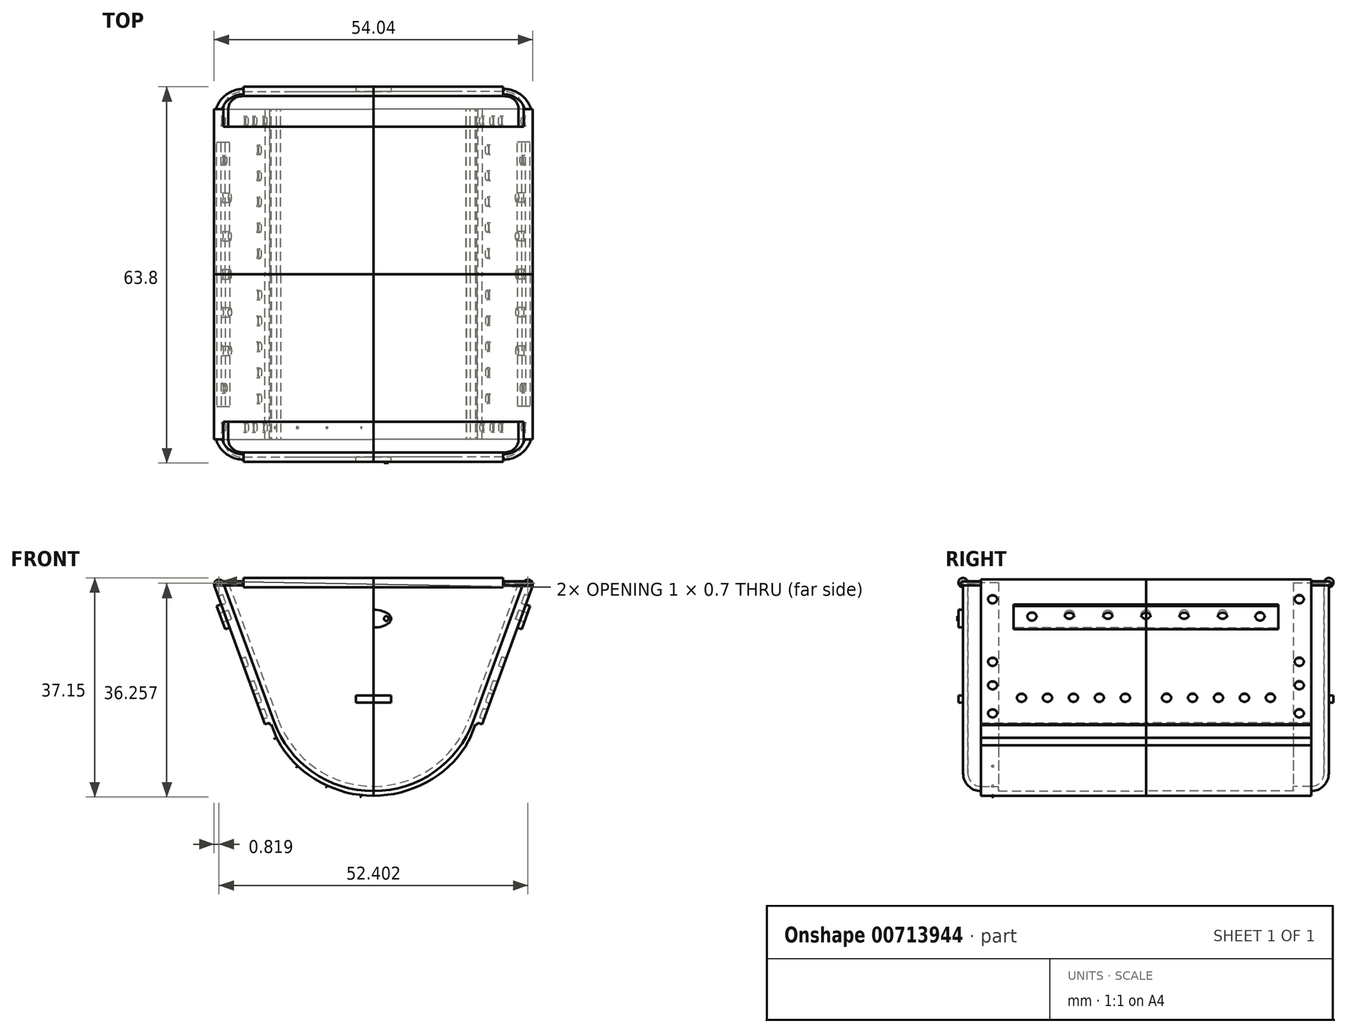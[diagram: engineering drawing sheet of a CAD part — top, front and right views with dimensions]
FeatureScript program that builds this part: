
annotation { "Feature Type Name" : "Feature", "Feature Type Description" : "" }
export const myFeature = defineFeature(function(context is Context, id is Id, definition is map)
    precondition{}
    {
        {
            var Q0;
            Q0=qCreatedBy(makeId("Right.planeOp"),FACE);
            var sketch = newSketch(context, id + "F0", { "sketchPlane" : qUnion([Q0])});
            skLineSegment(sketch, "E0.bottom", {"start": v(-15, -21) * mm, "end": v(-15, -21.8) * mm});
            skLineSegment(sketch, "E0.top", {"start": v(13, -21) * mm, "end": v(13, -21.8) * mm});
            skLineSegment(sketch, "E0.left", {"start": v(-15, -21) * mm, "end": v(13, -21) * mm});
            skLineSegment(sketch, "E0.right", {"start": v(-15, -21.8) * mm, "end": v(13, -21.8) * mm});
            skLineSegment(sketch, "E1.bottom", {"start": v(-15, -21) * mm, "end": v(-15, -20.2) * mm});
            skLineSegment(sketch, "E1.top", {"start": v(-12, -21) * mm, "end": v(-12, -20.2) * mm});
            skLineSegment(sketch, "E1.left", {"start": v(-15, -21) * mm, "end": v(-12, -21) * mm});
            skLineSegment(sketch, "E1.right", {"start": v(-15, -20.2) * mm, "end": v(-12, -20.2) * mm});
            skLineSegment(sketch, "E2.bottom", {"start": v(-15, -21) * mm, "end": v(-15, -18) * mm, "construction": true});
            skLineSegment(sketch, "E2.top", {"start": v(-15.62, -21) * mm, "end": v(-15.62, -18) * mm, "construction": true});
            skLineSegment(sketch, "E2.left", {"start": v(-15, -21) * mm, "end": v(-15.62, -21) * mm, "construction": true});
            skLineSegment(sketch, "E2.right", {"start": v(-15, -18) * mm, "end": v(-15.62, -18) * mm, "construction": true});
            skArc(sketch, "E3", {"start": v(-15, -21) * mm, "mid": v(-17.12, -20.12) * mm, "end": v(-18, -18) * mm});
            skArc(sketch, "E4", {"start": v(-15, -20.2) * mm, "mid": v(-16.56, -19.56) * mm, "end": v(-17.2, -18) * mm});
            skLineSegment(sketch, "E5.bottom", {"start": v(-17.2, -18) * mm, "end": v(-17.2, -3) * mm});
            skLineSegment(sketch, "E5.top", {"start": v(-18, -18) * mm, "end": v(-18, -3) * mm});
            skLineSegment(sketch, "E5.left", {"start": v(-17.2, -18) * mm, "end": v(-18, -18) * mm});
            skLineSegment(sketch, "E5.right", {"start": v(-17.2, -3) * mm, "end": v(-18, -3) * mm});
            skSolve(sketch);
        }
        {
            var Q0;
            Q0=makeQuery(id+"F0.imprint","IMPRINT",FACE,{"disambiguationData":[TD([[makeQuery(id+"F0.imprint","IMPRINT",EDGE,{"derivedFrom":sQuery(id+"F0.wireOp",EDGE,"E5.bottom")}),1.0]])]});
            var Q1;
            Q1=makeQuery(id+"F0.imprint","IMPRINT",FACE,{"disambiguationData":[TD([[makeQuery(id+"F0.imprint","IMPRINT",EDGE,{"derivedFrom":sQuery(id+"F0.wireOp",EDGE,"E1.bottom")}),1.0]])]});
            var Q2;
            Q2=makeQuery(id+"F0.imprint","IMPRINT",FACE,{"disambiguationData":[TD([[makeQuery(id+"F0.imprint","IMPRINT",EDGE,{"derivedFrom":sQuery(id+"F0.wireOp",EDGE,"E1.bottom")}),-1.0]])]});
            var Q3;
            Q3=makeQuery(id+"F0.imprint","IMPRINT",FACE,{"disambiguationData":[TD([[makeQuery(id+"F0.imprint","IMPRINT",EDGE,{"derivedFrom":sQuery(id+"F0.wireOp",EDGE,"E0.bottom")}),1.0]])]});
            var Q4;
            Q4=sQuery(id+"F0.wireOp",EDGE,"E5.right");
            revolve(context, id + "F1", {"surfaceOperationType" : NewSurfaceOperationType.NEW, "entities" : qUnion([Q0, Q1, Q2, Q3]), "axis" : qUnion([Q4]), "revolveType" : RevolveType.ONE_DIRECTION, "oppositeDirection" : true, "angle" : 70 * degree});
        }
        {
            var Q0;
            Q0=makeQuery(id+"F1.opRevolve","CAP_FACE",FACE,{"disambiguationData":[OSD([sQuery(id+"F0.wireOp",EDGE,"E0.bottom"),sQuery(id+"F0.wireOp",EDGE,"E0.top"),sQuery(id+"F0.wireOp",EDGE,"E0.left"),sQuery(id+"F0.wireOp",EDGE,"E0.right"),sQuery(id+"F0.wireOp",EDGE,"E1.top"),sQuery(id+"F0.wireOp",EDGE,"E1.right"),sQuery(id+"F0.wireOp",EDGE,"E3"),sQuery(id+"F0.wireOp",EDGE,"E4"),sQuery(id+"F0.wireOp",EDGE,"E5.bottom"),sQuery(id+"F0.wireOp",EDGE,"E5.top"),sQuery(id+"F0.wireOp",EDGE,"E5.right")])],"isStart":false});
            extrude(context, id + "F2", {"entities" : qUnion([Q0]), "operationType" : NewBodyOperationType.ADD, "depth" : 25 * mm, "offsetDistance" : 25 * mm});
        }
        {
            var Q0;
            {var subQ0=sQuery(id+"F0.wireOp",EDGE,"E0.bottom");Q0=makeQuery(id+"F2.boolean.opBoolean","MERGE",FACE,{"derivedFrom":[makeQuery(id+"F1.opRevolve","SWEPT_FACE",FACE,{"disambiguationData":[OSD([subQ0])]}),makeQuery(id+"F2.opExtrude","SWEPT_FACE",FACE,{"disambiguationData":[OSD([subQ0])]})]});}
            var sketch = newSketch(context, id + "F3", { "sketchPlane" : qUnion([Q0])});
            skLineSegment(sketch, "E6", {"start": v(-26.22, 14.06) * mm, "end": v(-17.67, -9.43) * mm});
            skLineSegment(sketch, "E7", {"start": v(-17.67, -9.43) * mm, "end": v(-17.3, -9.3) * mm});
            skLineSegment(sketch, "E8", {"start": v(-26.22, 14.06) * mm, "end": v(-17.3, -9.3) * mm});
            skSolve(sketch);
        }
        {
            var Q0;
            Q0=makeQuery(id+"F3.imprint","IMPRINT",FACE,{"disambiguationData":[TD([[makeQuery(id+"F3.imprint","IMPRINT",EDGE,{"derivedFrom":sQuery(id+"F3.wireOp",EDGE,"E6")}),1.0]])]});
            extrude(context, id + "F4", {"entities" : qUnion([Q0]), "oppositeDirection" : true, "depth" : 28 * mm, "offsetDistance" : 25 * mm});
        }
        {
            var Q0;
            Q0=makeQuery(id+"F2.opExtrude","SWEPT_FACE",FACE,{"disambiguationData":[OSD([sQuery(id+"F0.wireOp",EDGE,"E0.right")])]});
            var sketch = newSketch(context, id + "F5", { "sketchPlane" : qUnion([Q0])});
            skLineSegment(sketch, "E9.left", {"start": v(-13, 18.82) * mm, "end": v(-13, 14.65) * mm});
            skCircle(sketch, "E10", {"center": v(-13, 16.74) * mm, "radius": 0.8 * mm});
            skCircle(sketch, "E11.MirrorC", {"center": v(13, -1.04) * mm, "radius": 0.8 * mm});
            skCircle(sketch, "E12.MirrorC", {"center": v(13, 19.56) * mm, "radius": 0.8 * mm});
            skCircle(sketch, "E13.MirrorC", {"center": v(8.1, 1.78) * mm, "radius": 0.8 * mm});
            skCircle(sketch, "E14.MirrorC", {"center": v(13, 8.27) * mm, "radius": 0.8 * mm});
            skCircle(sketch, "E15.MirrorC", {"center": v(6.33, 16.74) * mm, "radius": 0.8 * mm});
            skCircle(sketch, "E16.MirrorC", {"center": v(13, 4.02) * mm, "radius": 0.8 * mm});
            skLineSegment(sketch, "E17.MirrorCS", {"start": v(13, 20.36) * mm, "end": v(13, -1.84) * mm});
            skCircle(sketch, "E18.MirrorC", {"center": v(-0.02, 16.74) * mm, "radius": 0.8 * mm});
            skCircle(sketch, "E19.MirrorC", {"center": v(-0.7, 1.78) * mm, "radius": 0.8 * mm});
            skLineSegment(sketch, "E20.MirrorCS", {"start": v(9.43, 18.82) * mm, "end": v(9.43, 14.65) * mm});
            skCircle(sketch, "E21.MirrorC", {"center": v(-5.1, 1.78) * mm, "radius": 0.8 * mm});
            skCircle(sketch, "E22.MirrorC", {"center": v(-9.5, 1.78) * mm, "radius": 0.8 * mm});
            skCircle(sketch, "E23.MirrorC", {"center": v(-6.54, 16.74) * mm, "radius": 0.8 * mm});
            skCircle(sketch, "E24.MirrorC", {"center": v(13, 15.05) * mm, "radius": 0.8 * mm});
            skCircle(sketch, "E25.MirrorC", {"center": v(3.7, 1.78) * mm, "radius": 0.8 * mm});
            skLineSegment(sketch, "E26.MirrorCS", {"start": v(-13, 18.82) * mm, "end": v(9.43, 18.82) * mm});
            skLineSegment(sketch, "E27.MirrorCS", {"start": v(13, 19.36) * mm, "end": v(13, -2.82) * mm, "construction": true});
            skPoint(sketch, "E28.MirrorP", {"position": v(9.43, 16.74) * mm});
            skLineSegment(sketch, "E29.MirrorCS", {"start": v(-13, 1.78) * mm, "end": v(-27.66, 1.78) * mm, "construction": true});
            skLineSegment(sketch, "E30.MirrorCS", {"start": v(12.5, 1.78) * mm, "end": v(8.1, 1.78) * mm, "construction": true});
            skLineSegment(sketch, "E31.MirrorCS", {"start": v(-13, 14.65) * mm, "end": v(9.43, 14.65) * mm});
            skSolve(sketch);
        }
        {
            var Q0;
            Q0=makeQuery(id+"F5.imprint","IMPRINT",FACE,{"disambiguationData":[TD([[makeQuery(id+"F5.imprint","IMPRINT",EDGE,{"derivedFrom":sQuery(id+"F5.wireOp",EDGE,"E15.MirrorC")}),1.0]])]});
            extrude(context, id + "F6", {"entities" : qUnion([Q0]), "operationType" : NewBodyOperationType.ADD, "depth" : .8 * mm, "offsetDistance" : 25 * mm});
        }
        {
            var Q0;
            {var subQ0=sQuery(id+"F5.wireOp",EDGE,"E17.MirrorCS");var subQ1=sQuery(id+"F5.wireOp",EDGE,"E12.MirrorC");var subQ2=makeQuery(id+"F5.imprint","INTERSECT",VERTEX,{"disambiguationData":[OD(0.0)],"derivedFrom":[subQ1,subQ0]});Q0=makeQuery(id+"F5.imprint","IMPRINT",FACE,{"disambiguationData":[TD([[makeQuery(id+"F5.imprint","IMPRINT",EDGE,{"disambiguationData":[TD([[subQ2,1.0]])],"derivedFrom":subQ1}),-1.0]])]});}
            var Q1;
            {var subQ0=sQuery(id+"F5.wireOp",EDGE,"E17.MirrorCS");var subQ1=sQuery(id+"F5.wireOp",EDGE,"E12.MirrorC");var subQ2=makeQuery(id+"F5.imprint","INTERSECT",VERTEX,{"disambiguationData":[OD(0.0)],"derivedFrom":[subQ1,subQ0]});Q1=makeQuery(id+"F5.imprint","IMPRINT",FACE,{"disambiguationData":[TD([[makeQuery(id+"F5.imprint","IMPRINT",EDGE,{"disambiguationData":[TD([[subQ2,-1.0]])],"derivedFrom":subQ1}),-1.0]])]});}
            var Q2;
            {var subQ0=sQuery(id+"F5.wireOp",EDGE,"E24.MirrorC");var subQ1=sQuery(id+"F5.wireOp",EDGE,"E17.MirrorCS");var subQ2=makeQuery(id+"F5.imprint","INTERSECT",VERTEX,{"disambiguationData":[OD(0.0)],"derivedFrom":[subQ1,subQ0]});Q2=makeQuery(id+"F5.imprint","IMPRINT",FACE,{"disambiguationData":[TD([[makeQuery(id+"F5.imprint","IMPRINT",EDGE,{"disambiguationData":[TD([[subQ2,-1.0]])],"derivedFrom":subQ1}),-1.0]])]});}
            var Q3;
            {var subQ0=sQuery(id+"F5.wireOp",EDGE,"E24.MirrorC");var subQ1=sQuery(id+"F5.wireOp",EDGE,"E17.MirrorCS");var subQ2=makeQuery(id+"F5.imprint","INTERSECT",VERTEX,{"disambiguationData":[OD(0.0)],"derivedFrom":[subQ1,subQ0]});Q3=makeQuery(id+"F5.imprint","IMPRINT",FACE,{"disambiguationData":[TD([[makeQuery(id+"F5.imprint","IMPRINT",EDGE,{"disambiguationData":[TD([[subQ2,-1.0]])],"derivedFrom":subQ1}),1.0]])]});}
            var Q4;
            {var subQ0=sQuery(id+"F5.wireOp",EDGE,"E17.MirrorCS");var subQ1=sQuery(id+"F5.wireOp",EDGE,"E14.MirrorC");var subQ2=makeQuery(id+"F5.imprint","INTERSECT",VERTEX,{"disambiguationData":[OD(0.0)],"derivedFrom":[subQ1,subQ0]});Q4=makeQuery(id+"F5.imprint","IMPRINT",FACE,{"disambiguationData":[TD([[makeQuery(id+"F5.imprint","IMPRINT",EDGE,{"disambiguationData":[TD([[subQ2,1.0]])],"derivedFrom":subQ1}),-1.0]])]});}
            var Q5;
            {var subQ0=sQuery(id+"F5.wireOp",EDGE,"E17.MirrorCS");var subQ1=sQuery(id+"F5.wireOp",EDGE,"E14.MirrorC");var subQ2=makeQuery(id+"F5.imprint","INTERSECT",VERTEX,{"disambiguationData":[OD(0.0)],"derivedFrom":[subQ1,subQ0]});Q5=makeQuery(id+"F5.imprint","IMPRINT",FACE,{"disambiguationData":[TD([[makeQuery(id+"F5.imprint","IMPRINT",EDGE,{"disambiguationData":[TD([[subQ2,-1.0]])],"derivedFrom":subQ1}),-1.0]])]});}
            var Q6;
            {var subQ0=sQuery(id+"F5.wireOp",EDGE,"E17.MirrorCS");var subQ1=sQuery(id+"F5.wireOp",EDGE,"E16.MirrorC");var subQ2=makeQuery(id+"F5.imprint","INTERSECT",VERTEX,{"disambiguationData":[OD(0.0)],"derivedFrom":[subQ1,subQ0]});Q6=makeQuery(id+"F5.imprint","IMPRINT",FACE,{"disambiguationData":[TD([[makeQuery(id+"F5.imprint","IMPRINT",EDGE,{"disambiguationData":[TD([[subQ2,1.0]])],"derivedFrom":subQ1}),-1.0]])]});}
            var Q7;
            {var subQ0=sQuery(id+"F5.wireOp",EDGE,"E17.MirrorCS");var subQ1=sQuery(id+"F5.wireOp",EDGE,"E16.MirrorC");var subQ2=makeQuery(id+"F5.imprint","INTERSECT",VERTEX,{"disambiguationData":[OD(0.0)],"derivedFrom":[subQ1,subQ0]});Q7=makeQuery(id+"F5.imprint","IMPRINT",FACE,{"disambiguationData":[TD([[makeQuery(id+"F5.imprint","IMPRINT",EDGE,{"disambiguationData":[TD([[subQ2,-1.0]])],"derivedFrom":subQ1}),-1.0]])]});}
            var Q8;
            {var subQ0=sQuery(id+"F5.wireOp",EDGE,"E17.MirrorCS");var subQ1=sQuery(id+"F5.wireOp",EDGE,"E11.MirrorC");var subQ2=makeQuery(id+"F5.imprint","INTERSECT",VERTEX,{"disambiguationData":[OD(0.0)],"derivedFrom":[subQ1,subQ0]});Q8=makeQuery(id+"F5.imprint","IMPRINT",FACE,{"disambiguationData":[TD([[makeQuery(id+"F5.imprint","IMPRINT",EDGE,{"disambiguationData":[TD([[subQ2,-1.0]])],"derivedFrom":subQ1}),-1.0]])]});}
            var Q9;
            {var subQ0=sQuery(id+"F5.wireOp",EDGE,"E17.MirrorCS");var subQ1=sQuery(id+"F5.wireOp",EDGE,"E11.MirrorC");var subQ2=makeQuery(id+"F5.imprint","INTERSECT",VERTEX,{"disambiguationData":[OD(0.0)],"derivedFrom":[subQ1,subQ0]});Q9=makeQuery(id+"F5.imprint","IMPRINT",FACE,{"disambiguationData":[TD([[makeQuery(id+"F5.imprint","IMPRINT",EDGE,{"disambiguationData":[TD([[subQ2,1.0]])],"derivedFrom":subQ1}),-1.0]])]});}
            var Q10;
            Q10=makeQuery(id+"F5.imprint","IMPRINT",FACE,{"disambiguationData":[TD([[makeQuery(id+"F5.imprint","IMPRINT",EDGE,{"derivedFrom":sQuery(id+"F5.wireOp",EDGE,"E13.MirrorC")}),-1.0]])]});
            var Q11;
            Q11=makeQuery(id+"F5.imprint","IMPRINT",FACE,{"disambiguationData":[TD([[makeQuery(id+"F5.imprint","IMPRINT",EDGE,{"derivedFrom":sQuery(id+"F5.wireOp",EDGE,"E25.MirrorC")}),-1.0]])]});
            var Q12;
            Q12=makeQuery(id+"F5.imprint","IMPRINT",FACE,{"disambiguationData":[TD([[makeQuery(id+"F5.imprint","IMPRINT",EDGE,{"derivedFrom":sQuery(id+"F5.wireOp",EDGE,"E19.MirrorC")}),-1.0]])]});
            var Q13;
            Q13=makeQuery(id+"F5.imprint","IMPRINT",FACE,{"disambiguationData":[TD([[makeQuery(id+"F5.imprint","IMPRINT",EDGE,{"derivedFrom":sQuery(id+"F5.wireOp",EDGE,"E21.MirrorC")}),-1.0]])]});
            var Q14;
            Q14=makeQuery(id+"F5.imprint","IMPRINT",FACE,{"disambiguationData":[TD([[makeQuery(id+"F5.imprint","IMPRINT",EDGE,{"derivedFrom":sQuery(id+"F5.wireOp",EDGE,"E22.MirrorC")}),-1.0]])]});
            var Q15;
            Q15=makeQuery(id+"F5.imprint","IMPRINT",FACE,{"disambiguationData":[TD([[makeQuery(id+"F5.imprint","IMPRINT",EDGE,{"derivedFrom":sQuery(id+"F5.wireOp",EDGE,"E15.MirrorC")}),1.0]])]});
            extrude(context, id + "F7", {"entities" : qUnion([Q0, Q1, Q2, Q3, Q4, Q5, Q6, Q7, Q8, Q9, Q10, Q11, Q12, Q13, Q14, Q15]), "operationType" : NewBodyOperationType.ADD, "depth" : .8 * mm, "offsetDistance" : 25 * mm});
        }
        {
            var Q0;
            {var subQ0=sQuery(id+"F0.wireOp",EDGE,"E0.bottom");Q0=makeQuery(id+"F2.boolean.opBoolean","MERGE",FACE,{"derivedFrom":[makeQuery(id+"F1.opRevolve","SWEPT_FACE",FACE,{"disambiguationData":[OSD([subQ0])]}),makeQuery(id+"F2.opExtrude","SWEPT_FACE",FACE,{"disambiguationData":[OSD([subQ0])]})]});}
            var sketch = newSketch(context, id + "F8", { "sketchPlane" : qUnion([Q0])});
            skLineSegment(sketch, "E32", {"start": v(-26.22, 14.06) * mm, "end": v(-25.65, 14.27) * mm, "construction": true});
            skLineSegment(sketch, "E33", {"start": v(-26.22, 14.06) * mm, "end": v(-25.46, 14.34) * mm});
            skLineSegment(sketch, "E34", {"start": v(-26.22, 14.06) * mm, "end": v(-17.17, -10.79) * mm});
            skLineSegment(sketch, "E35", {"start": v(-25.46, 14.34) * mm, "end": v(-27.63, 13.55) * mm, "construction": true});
            skLineSegment(sketch, "E36", {"start": v(-27.63, 13.55) * mm, "end": v(-37.62, 13.34) * mm, "construction": true});
            skCircle(sketch, "E37", {"center": v(-26.22, 14.06) * mm, "radius": 0.8 * mm});
            skSolve(sketch);
        }
        {
            var Q0;
            Q0=makeQuery(id+"F8.imprint","IMPRINT",FACE,{"disambiguationData":[TD([[makeQuery(id+"F8.imprint","IMPRINT",EDGE,{"derivedFrom":sQuery(id+"F8.wireOp",EDGE,"LhP0sfN7-OzdZ-2R5g-prXg-6koaKuXarlO9")}),-1.0]])]});
            var Q1;
            Q1=makeQuery(id+"F8.imprint","IMPRINT",FACE,{"disambiguationData":[TD([[makeQuery(id+"F8.imprint","IMPRINT",EDGE,{"derivedFrom":sQuery(id+"F8.wireOp",EDGE,"LhP0sfN7-OzdZ-2R5g-prXg-6koaKuXarlO9")}),1.0]])]});
            var Q2;
            {var subQ0=sQuery(id+"F8.wireOp",EDGE,"E33");Q2=makeQuery(id+"F8.imprint","IMPRINT",FACE,{"disambiguationData":[TD([[makeQuery(id+"F8.imprint","IMPRINT",EDGE,{"derivedFrom":subQ0}),-1.0]])]});}
            extrude(context, id + "F9", {"entities" : qUnion([Q0, Q1, Q2]), "operationType" : NewBodyOperationType.ADD, "oppositeDirection" : true, "depth" : 28 * mm, "offsetDistance" : 25 * mm});
        }
        {
            var Q0;
            {var subQ0=sQuery(id+"F0.wireOp",EDGE,"E0.top");Q0=makeQuery(id+"F2.boolean.opBoolean","MERGE",FACE,{"derivedFrom":[makeQuery(id+"F1.opRevolve","SWEPT_FACE",FACE,{"disambiguationData":[OSD([subQ0])]}),makeQuery(id+"F2.opExtrude","SWEPT_FACE",FACE,{"disambiguationData":[OSD([subQ0])]})]});}
            var sketch = newSketch(context, id + "F10", { "sketchPlane" : qUnion([Q0])});
            skLineSegment(sketch, "E38.bottom", {"start": v(25.46, 14.34) * mm, "end": v(5.72, 14.34) * mm});
            skLineSegment(sketch, "E38.top", {"start": v(25.46, 20.8) * mm, "end": v(5.72, 20.8) * mm});
            skLineSegment(sketch, "E38.left", {"start": v(25.46, 14.34) * mm, "end": v(25.46, 20.8) * mm});
            skLineSegment(sketch, "E38.right", {"start": v(5.72, 14.34) * mm, "end": v(5.72, 20.8) * mm});
            skSolve(sketch);
        }
        {
            var Q0;
            {var subQ0=sQuery(id+"F0.wireOp",EDGE,"E5.top");Q0=makeQuery(id+"F2.boolean.opBoolean","MERGE",FACE,{"derivedFrom":[makeQuery(id+"F1.opRevolve","SWEPT_FACE",FACE,{"disambiguationData":[OSD([subQ0])]}),makeQuery(id+"F2.opExtrude","SWEPT_FACE",FACE,{"disambiguationData":[OSD([subQ0])]})]});}
            var sketch = newSketch(context, id + "F11", { "sketchPlane" : qUnion([Q0])});
            skLineSegment(sketch, "E39.bottom", {"start": v(0, -3) * mm, "end": v(-6.31, -3) * mm});
            skLineSegment(sketch, "E39.top", {"start": v(0, 14.34) * mm, "end": v(-6.31, 14.34) * mm});
            skLineSegment(sketch, "E39.left", {"start": v(0, -3) * mm, "end": v(0, 14.34) * mm});
            skLineSegment(sketch, "E39.right", {"start": v(-6.31, -3) * mm, "end": v(-6.31, 14.34) * mm});
            skSolve(sketch);
        }
        {
            var Q0;
            {var subQ0=sQuery(id+"F11.wireOp",EDGE,"E39.top");Q0=makeQuery(id+"F11.imprint","IMPRINT",FACE,{"disambiguationData":[TD([[makeQuery(id+"F11.imprint","IMPRINT",EDGE,{"derivedFrom":subQ0}),1.0]])]});}
            extrude(context, id + "F12", {"entities" : qUnion([Q0]), "operationType" : NewBodyOperationType.ADD, "oppositeDirection" : true, "depth" : .8 * mm, "offsetDistance" : 25 * mm});
        }
        {
            var Q0;
            Q0=makeQuery(id+"F10.imprint","IMPRINT",FACE,{"disambiguationData":[TD([[makeQuery(id+"F10.imprint","IMPRINT",EDGE,{"derivedFrom":sQuery(id+"F10.wireOp",EDGE,"E38.bottom")}),-1.0]])]});
            extrude(context, id + "F13", {"entities" : qUnion([Q0]), "operationType" : NewBodyOperationType.REMOVE, "oppositeDirection" : true, "depth" : 50 * mm, "offsetDistance" : 25 * mm});
        }
        {
            var Q0;
            {var subQ0=sQuery(id+"F0.wireOp",EDGE,"E5.top");Q0=makeQuery(id+"F12.boolean.opBoolean","MERGE",FACE,{"derivedFrom":[makeQuery(id+"F2.boolean.opBoolean","MERGE",FACE,{"derivedFrom":[makeQuery(id+"F1.opRevolve","SWEPT_FACE",FACE,{"disambiguationData":[OSD([subQ0])]}),makeQuery(id+"F2.opExtrude","SWEPT_FACE",FACE,{"disambiguationData":[OSD([subQ0])]})]}),makeQuery(id+"F12.opExtrude","CAP_FACE",FACE,{"disambiguationData":[OSD([subQ0,sQuery(id+"F0.wireOp",EDGE,"E5.right"),sQuery(id+"F11.wireOp",EDGE,"E39.top"),sQuery(id+"F11.wireOp",EDGE,"E39.left")])],"isStart":true})]});}
            var sketch = newSketch(context, id + "F14", { "sketchPlane" : qUnion([Q0])});
            skEllipse(sketch, "E40", {"center": v(0, 8.24) * mm, "majorRadius": 3 * mm, "minorRadius": 1.5 * mm, "majorAxis": v(1, 0)});
            skCircle(sketch, "E41", {"center": v(2.18, 8.25) * mm, "radius": 0.4 * mm});
            skLineSegment(sketch, "E42.top", {"start": v(0, -4.8) * mm, "end": v(-3, -4.8) * mm});
            skLineSegment(sketch, "E42.left", {"start": v(0, -3) * mm, "end": v(0, -4.8) * mm});
            skLineSegment(sketch, "E43.top", {"start": v(0, -6) * mm, "end": v(-3, -6) * mm});
            skLineSegment(sketch, "E43.left", {"start": v(0, -3.9) * mm, "end": v(0, -6) * mm});
            skLineSegment(sketch, "E44", {"start": v(-3, -4.8) * mm, "end": v(-3, -6) * mm});
            skSolve(sketch);
        }
        {
            var Q0;
            {var subQ0=sQuery(id+"F14.wireOp",EDGE,"E40");var subQ1=makeQuery(id+"F12.boolean.opBoolean","MERGE",EDGE,{"derivedFrom":[makeQuery(id+"F1.opRevolve","CAP_EDGE",EDGE,{"disambiguationData":[OSD([sQuery(id+"F0.wireOp",EDGE,"E5.top")])],"isStart":true}),makeQuery(id+"F12.opExtrude","CAP_EDGE",EDGE,{"disambiguationData":[OSD([sQuery(id+"F11.wireOp",EDGE,"E39.left")])],"isStart":true})]});var subQ2=makeQuery(id+"F14.imprint","INTERSECT",VERTEX,{"disambiguationData":[OD(0.0)],"derivedFrom":[subQ1,subQ0]});Q0=makeQuery(id+"F14.imprint","IMPRINT",FACE,{"disambiguationData":[TD([[makeQuery(id+"F14.imprint","IMPRINT",EDGE,{"disambiguationData":[TD([[subQ2,1.0]])],"derivedFrom":subQ0}),1.0]])]});}
            var Q1;
            Q1=makeQuery(id+"F14.imprint","IMPRINT",FACE,{"disambiguationData":[TD([[makeQuery(id+"F14.imprint","IMPRINT",EDGE,{"derivedFrom":sQuery(id+"F14.wireOp",EDGE,"E42.bottom")}),1.0]])]});
            var Q2;
            {var subQ0=sQuery(id+"F14.wireOp",EDGE,"E42.top");Q2=makeQuery(id+"F14.imprint","IMPRINT",FACE,{"disambiguationData":[TD([[makeQuery(id+"F14.imprint","IMPRINT",EDGE,{"derivedFrom":subQ0}),1.0]])]});}
            extrude(context, id + "F15", {"entities" : qUnion([Q0, Q1, Q2]), "operationType" : NewBodyOperationType.ADD, "depth" : .8 * mm, "offsetDistance" : 25 * mm});
        }
        {
            var Q0;
            Q0=makeQuery(id+"F7.opExtrude","CAP_EDGE",EDGE,{"disambiguationData":[OSD([sQuery(id+"F5.wireOp",EDGE,"E12.MirrorC")])],"isStart":false});
            var Q1;
            Q1=makeQuery(id+"F7.opExtrude","CAP_EDGE",EDGE,{"disambiguationData":[OSD([sQuery(id+"F5.wireOp",EDGE,"E24.MirrorC")])],"isStart":false});
            var Q2;
            Q2=makeQuery(id+"F7.opExtrude","CAP_EDGE",EDGE,{"disambiguationData":[OSD([sQuery(id+"F5.wireOp",EDGE,"E14.MirrorC")])],"isStart":false});
            var Q3;
            Q3=makeQuery(id+"F7.opExtrude","CAP_EDGE",EDGE,{"disambiguationData":[OSD([sQuery(id+"F5.wireOp",EDGE,"E16.MirrorC")])],"isStart":false});
            var Q4;
            Q4=makeQuery(id+"F7.opExtrude","CAP_EDGE",EDGE,{"disambiguationData":[OSD([sQuery(id+"F5.wireOp",EDGE,"E11.MirrorC")])],"isStart":false});
            var Q5;
            Q5=makeQuery(id+"F7.opExtrude","CAP_EDGE",EDGE,{"disambiguationData":[OSD([sQuery(id+"F5.wireOp",EDGE,"E13.MirrorC")])],"isStart":false});
            var Q6;
            Q6=makeQuery(id+"F7.opExtrude","CAP_EDGE",EDGE,{"disambiguationData":[OSD([sQuery(id+"F5.wireOp",EDGE,"E25.MirrorC")])],"isStart":false});
            var Q7;
            Q7=makeQuery(id+"F7.opExtrude","CAP_EDGE",EDGE,{"disambiguationData":[OSD([sQuery(id+"F5.wireOp",EDGE,"E19.MirrorC")])],"isStart":false});
            var Q8;
            Q8=makeQuery(id+"F7.opExtrude","CAP_EDGE",EDGE,{"disambiguationData":[OSD([sQuery(id+"F5.wireOp",EDGE,"E21.MirrorC")])],"isStart":false});
            var Q9;
            Q9=makeQuery(id+"F7.opExtrude","CAP_EDGE",EDGE,{"disambiguationData":[OSD([sQuery(id+"F5.wireOp",EDGE,"E22.MirrorC")])],"isStart":false});
            fillet(context, id + "F16", {"entities" : qUnion([Q0, Q1, Q2, Q3, Q4, Q5, Q6, Q7, Q8, Q9]), "radius" : .6 * mm, "tangentPropagation" : true, "defaultsChanged" : false, "vertexSettings" : [], "allowEdgeOverflow" : false});
        }
        {
            var Q0;
            Q0=makeQuery(id+"F14.imprint","IMPRINT",FACE,{"disambiguationData":[TD([[makeQuery(id+"F14.imprint","IMPRINT",EDGE,{"derivedFrom":sQuery(id+"F14.wireOp",EDGE,"E41")}),-1.0]])]});
            extrude(context, id + "F17", {"entities" : qUnion([Q0]), "operationType" : NewBodyOperationType.ADD, "depth" : .4 * mm, "offsetDistance" : 25 * mm});
        }
        {
            var Q0;
            Q0=makeQuery(id+"F14.imprint","IMPRINT",FACE,{"disambiguationData":[TD([[makeQuery(id+"F14.imprint","IMPRINT",EDGE,{"derivedFrom":sQuery(id+"F14.wireOp",EDGE,"E41")}),1.0]])]});
            extrude(context, id + "F18", {"entities" : qUnion([Q0]), "operationType" : NewBodyOperationType.ADD, "depth" : 1 * mm, "offsetDistance" : 25 * mm});
        }
        {
            var Q0;
            {var subQ0=sQuery(id+"F0.wireOp",EDGE,"E0.bottom");Q0=makeQuery(id+"F8.imprint","IMPRINT",FACE,{"disambiguationData":[TD([[makeQuery(id+"F8.imprint","IMPRINT",EDGE,{"derivedFrom":makeQuery(id+"F1.opRevolve","CAP_EDGE",EDGE,{"disambiguationData":[OSD([subQ0])],"isStart":true})}),-1.0]])]});}
            var sketch = newSketch(context, id + "F19", { "sketchPlane" : qUnion([Q0])});
            skLineSegment(sketch, "E45.bottom", {"start": v(-18.27, -10.18) * mm, "end": v(-17.61, -10.18) * mm});
            skLineSegment(sketch, "E45.top", {"start": v(-18.27, -12.3) * mm, "end": v(-17.61, -12.3) * mm});
            skLineSegment(sketch, "E45.left", {"start": v(-18.27, -10.18) * mm, "end": v(-18.27, -12.3) * mm});
            skLineSegment(sketch, "E45.right", {"start": v(-17.61, -10.18) * mm, "end": v(-17.61, -12.3) * mm});
            skLineSegment(sketch, "E46", {"start": v(-18.27, -10.18) * mm, "end": v(-17.3, -9.65) * mm});
            skLineSegment(sketch, "E47", {"start": v(-17.3, -9.65) * mm, "end": v(-16.42, -11.98) * mm});
            skLineSegment(sketch, "E48", {"start": v(-16.42, -11.98) * mm, "end": v(-15.72, -13.26) * mm});
            skLineSegment(sketch, "E49", {"start": v(-15.72, -13.26) * mm, "end": v(-17.61, -12.3) * mm});
            skSolve(sketch);
        }
        {
            var Q0;
            {var subQ4=sQuery(id+"F19.wireOp",EDGE,"E47");Q0=makeQuery(id+"F19.imprint","IMPRINT",FACE,{"disambiguationData":[TD([[makeQuery(id+"F19.imprint","IMPRINT",EDGE,{"derivedFrom":subQ4}),-1.0]])]});}
            extrude(context, id + "F20", {"entities" : qUnion([Q0]), "operationType" : NewBodyOperationType.REMOVE, "oppositeDirection" : true, "depth" : 40 * mm, "offsetDistance" : 25 * mm});
        }
        {
            var Q0;
            {var subQ4=sQuery(id+"F0.wireOp",EDGE,"E0.right");var subQ5=sQuery(id+"F0.wireOp",EDGE,"E0.top");var subQ8=sQuery(id+"F0.wireOp",EDGE,"E1.right");var subQ12=sQuery(id+"F0.wireOp",EDGE,"E5.bottom");var subQ13=sQuery(id+"F0.wireOp",EDGE,"E5.top");var subQ14=sQuery(id+"F0.wireOp",EDGE,"E1.top");var subQ15=sQuery(id+"F0.wireOp",EDGE,"E0.left");var subQ16=sQuery(id+"F11.wireOp",EDGE,"E39.left");var subQ18=sQuery(id+"F0.wireOp",EDGE,"E5.right");var subQ19=sQuery(id+"F0.wireOp",EDGE,"E0.bottom");var subQ20=sQuery(id+"F0.wireOp",EDGE,"E3");var subQ21=sQuery(id+"F0.wireOp",EDGE,"E4");Q0=makeQuery(id+"F17.boolean.opBoolean","SPLIT",FACE,{"disambiguationData":[TD([makeQuery(id+"F1.opRevolve","SWEPT_FACE",FACE,{"disambiguationData":[OSD([subQ19])]})])],"derivedFrom":makeQuery(id+"F15.boolean.opBoolean","MERGE",FACE,{"derivedFrom":[makeQuery(id+"F12.boolean.opBoolean","MERGE",FACE,{"derivedFrom":[makeQuery(id+"F1.opRevolve","CAP_FACE",FACE,{"disambiguationData":[OSD([subQ19,subQ5,subQ15,subQ4,subQ14,subQ8,subQ20,subQ21,subQ12,subQ13,subQ18])],"isStart":true}),makeQuery(id+"F12.opExtrude","SWEPT_FACE",FACE,{"disambiguationData":[OSD([subQ16])]})]}),makeQuery(id+"F15.opExtrude","SWEPT_FACE",FACE,{"disambiguationData":[OSD([subQ13,subQ16])]})]})});}
            var sketch = newSketch(context, id + "F21", { "sketchPlane" : qUnion([Q0])});
            skCircle(sketch, "E50", {"center": v(-18, 14.34) * mm, "radius": 0.8 * mm});
            skSolve(sketch);
        }
        {
            var Q0;
            {var subQ1=sQuery(id+"F11.wireOp",EDGE,"E39.left");var subQ3=sQuery(id+"F11.wireOp",EDGE,"E39.top");var subQ4=makeQuery(id+"F12.opExtrude","SWEPT_EDGE",EDGE,{"disambiguationData":[OSD([subQ3,subQ1])]});Q0=makeQuery(id+"F21.imprint","IMPRINT",FACE,{"disambiguationData":[TD([[makeQuery(id+"F21.imprint","IMPRINT",EDGE,{"derivedFrom":subQ4}),-1.0]])]});}
            extrude(context, id + "F22", {"entities" : qUnion([Q0]), "operationType" : NewBodyOperationType.ADD, "oppositeDirection" : true, "depth" : 22 * mm, "offsetDistance" : 25 * mm});
        }
        {
            var Q0;
            Q0=makeQuery(id+"F13.boolean.opBoolean","COPY",FACE,{"derivedFrom":makeQuery(id+"F13.opExtrude","SWEPT_FACE",FACE,{"disambiguationData":[OSD([sQuery(id+"F10.wireOp",EDGE,"E38.bottom")])]})});
            var sketch = newSketch(context, id + "F23", { "sketchPlane" : qUnion([Q0])});
            skArc(sketch, "E51", {"start": v(-26.25, -15.01) * mm, "mid": v(-24.61, -17.2) * mm, "end": v(-22, -18) * mm});
            skSolve(sketch);
        }
        {
            var Q0;
            {var subQ0=sQuery(id+"F8.wireOp",EDGE,"E33");Q0=makeQuery(id+"F8.imprint","IMPRINT",FACE,{"disambiguationData":[TD([[makeQuery(id+"F8.imprint","IMPRINT",EDGE,{"derivedFrom":subQ0}),-1.0]])]});}
            var sketch = newSketch(context, id + "F24", { "sketchPlane" : qUnion([Q0])});
            skCircle(sketch, "E52", {"center": v(-26.19, 14.08) * mm, "radius": 0.52 * mm});
            skSolve(sketch);
        }
        {
            var Q0;
            {var subQ0=sQuery(id+"F24.wireOp",EDGE,"E52");var subQ1=sQuery(id+"F8.wireOp",EDGE,"E33");var subQ2=makeQuery(id+"F8.imprint","IMPRINT",EDGE,{"derivedFrom":subQ1});var subQ3=makeQuery(id+"F24.imprint","INTERSECT",VERTEX,{"derivedFrom":[subQ2,subQ0]});Q0=makeQuery(id+"F24.imprint","IMPRINT",FACE,{"disambiguationData":[TD([[makeQuery(id+"F24.imprint","IMPRINT",EDGE,{"disambiguationData":[TD([[subQ3,-1.0]])],"derivedFrom":subQ0}),1.0]])]});}
            var Q1;
            Q1=sQuery(id+"F23.wireOp",EDGE,"E51");
            sweep(context, id + "F25", {"operationType" : NewBodyOperationType.ADD, "profiles" : qUnion([Q0]), "path" : qUnion([Q1])});
        }
        {
            var Q0;
            Q0=makeQuery(id+"F5.imprint","IMPRINT",FACE,{"disambiguationData":[TD([[makeQuery(id+"F5.imprint","IMPRINT",EDGE,{"derivedFrom":sQuery(id+"F5.wireOp",EDGE,"E22.MirrorC")}),-1.0]])]});
            var Q1;
            Q1=makeQuery(id+"F5.imprint","IMPRINT",FACE,{"disambiguationData":[TD([[makeQuery(id+"F5.imprint","IMPRINT",EDGE,{"derivedFrom":sQuery(id+"F5.wireOp",EDGE,"E21.MirrorC")}),-1.0]])]});
            var Q2;
            Q2=makeQuery(id+"F5.imprint","IMPRINT",FACE,{"disambiguationData":[TD([[makeQuery(id+"F5.imprint","IMPRINT",EDGE,{"derivedFrom":sQuery(id+"F5.wireOp",EDGE,"E19.MirrorC")}),-1.0]])]});
            var Q3;
            Q3=makeQuery(id+"F5.imprint","IMPRINT",FACE,{"disambiguationData":[TD([[makeQuery(id+"F5.imprint","IMPRINT",EDGE,{"derivedFrom":sQuery(id+"F5.wireOp",EDGE,"E25.MirrorC")}),-1.0]])]});
            var Q4;
            Q4=makeQuery(id+"F5.imprint","IMPRINT",FACE,{"disambiguationData":[TD([[makeQuery(id+"F5.imprint","IMPRINT",EDGE,{"derivedFrom":sQuery(id+"F5.wireOp",EDGE,"E13.MirrorC")}),-1.0]])]});
            var Q5;
            {var subQ0=sQuery(id+"F5.wireOp",EDGE,"E17.MirrorCS");var subQ1=sQuery(id+"F5.wireOp",EDGE,"E11.MirrorC");var subQ2=makeQuery(id+"F5.imprint","INTERSECT",VERTEX,{"disambiguationData":[OD(0.0)],"derivedFrom":[subQ1,subQ0]});Q5=makeQuery(id+"F5.imprint","IMPRINT",FACE,{"disambiguationData":[TD([[makeQuery(id+"F5.imprint","IMPRINT",EDGE,{"disambiguationData":[TD([[subQ2,-1.0]])],"derivedFrom":subQ1}),-1.0]])]});}
            var Q6;
            {var subQ0=sQuery(id+"F5.wireOp",EDGE,"E17.MirrorCS");var subQ1=sQuery(id+"F5.wireOp",EDGE,"E11.MirrorC");var subQ2=makeQuery(id+"F5.imprint","INTERSECT",VERTEX,{"disambiguationData":[OD(0.0)],"derivedFrom":[subQ1,subQ0]});Q6=makeQuery(id+"F5.imprint","IMPRINT",FACE,{"disambiguationData":[TD([[makeQuery(id+"F5.imprint","IMPRINT",EDGE,{"disambiguationData":[TD([[subQ2,1.0]])],"derivedFrom":subQ1}),-1.0]])]});}
            var Q7;
            {var subQ0=sQuery(id+"F5.wireOp",EDGE,"E17.MirrorCS");var subQ1=sQuery(id+"F5.wireOp",EDGE,"E16.MirrorC");var subQ2=makeQuery(id+"F5.imprint","INTERSECT",VERTEX,{"disambiguationData":[OD(0.0)],"derivedFrom":[subQ1,subQ0]});Q7=makeQuery(id+"F5.imprint","IMPRINT",FACE,{"disambiguationData":[TD([[makeQuery(id+"F5.imprint","IMPRINT",EDGE,{"disambiguationData":[TD([[subQ2,-1.0]])],"derivedFrom":subQ1}),-1.0]])]});}
            var Q8;
            {var subQ0=sQuery(id+"F5.wireOp",EDGE,"E17.MirrorCS");var subQ1=sQuery(id+"F5.wireOp",EDGE,"E16.MirrorC");var subQ2=makeQuery(id+"F5.imprint","INTERSECT",VERTEX,{"disambiguationData":[OD(0.0)],"derivedFrom":[subQ1,subQ0]});Q8=makeQuery(id+"F5.imprint","IMPRINT",FACE,{"disambiguationData":[TD([[makeQuery(id+"F5.imprint","IMPRINT",EDGE,{"disambiguationData":[TD([[subQ2,1.0]])],"derivedFrom":subQ1}),-1.0]])]});}
            var Q9;
            {var subQ0=sQuery(id+"F5.wireOp",EDGE,"E17.MirrorCS");var subQ1=sQuery(id+"F5.wireOp",EDGE,"E14.MirrorC");var subQ2=makeQuery(id+"F5.imprint","INTERSECT",VERTEX,{"disambiguationData":[OD(0.0)],"derivedFrom":[subQ1,subQ0]});Q9=makeQuery(id+"F5.imprint","IMPRINT",FACE,{"disambiguationData":[TD([[makeQuery(id+"F5.imprint","IMPRINT",EDGE,{"disambiguationData":[TD([[subQ2,-1.0]])],"derivedFrom":subQ1}),-1.0]])]});}
            var Q10;
            {var subQ0=sQuery(id+"F5.wireOp",EDGE,"E17.MirrorCS");var subQ1=sQuery(id+"F5.wireOp",EDGE,"E14.MirrorC");var subQ2=makeQuery(id+"F5.imprint","INTERSECT",VERTEX,{"disambiguationData":[OD(0.0)],"derivedFrom":[subQ1,subQ0]});Q10=makeQuery(id+"F5.imprint","IMPRINT",FACE,{"disambiguationData":[TD([[makeQuery(id+"F5.imprint","IMPRINT",EDGE,{"disambiguationData":[TD([[subQ2,1.0]])],"derivedFrom":subQ1}),-1.0]])]});}
            var Q11;
            {var subQ0=sQuery(id+"F5.wireOp",EDGE,"E24.MirrorC");var subQ1=sQuery(id+"F5.wireOp",EDGE,"E17.MirrorCS");var subQ2=makeQuery(id+"F5.imprint","INTERSECT",VERTEX,{"disambiguationData":[OD(0.0)],"derivedFrom":[subQ1,subQ0]});Q11=makeQuery(id+"F5.imprint","IMPRINT",FACE,{"disambiguationData":[TD([[makeQuery(id+"F5.imprint","IMPRINT",EDGE,{"disambiguationData":[TD([[subQ2,-1.0]])],"derivedFrom":subQ1}),1.0]])]});}
            var Q12;
            {var subQ0=sQuery(id+"F5.wireOp",EDGE,"E24.MirrorC");var subQ1=sQuery(id+"F5.wireOp",EDGE,"E17.MirrorCS");var subQ2=makeQuery(id+"F5.imprint","INTERSECT",VERTEX,{"disambiguationData":[OD(0.0)],"derivedFrom":[subQ1,subQ0]});Q12=makeQuery(id+"F5.imprint","IMPRINT",FACE,{"disambiguationData":[TD([[makeQuery(id+"F5.imprint","IMPRINT",EDGE,{"disambiguationData":[TD([[subQ2,-1.0]])],"derivedFrom":subQ1}),-1.0]])]});}
            var Q13;
            {var subQ0=sQuery(id+"F5.wireOp",EDGE,"E17.MirrorCS");var subQ1=sQuery(id+"F5.wireOp",EDGE,"E12.MirrorC");var subQ2=makeQuery(id+"F5.imprint","INTERSECT",VERTEX,{"disambiguationData":[OD(0.0)],"derivedFrom":[subQ1,subQ0]});Q13=makeQuery(id+"F5.imprint","IMPRINT",FACE,{"disambiguationData":[TD([[makeQuery(id+"F5.imprint","IMPRINT",EDGE,{"disambiguationData":[TD([[subQ2,-1.0]])],"derivedFrom":subQ1}),-1.0]])]});}
            var Q14;
            {var subQ0=sQuery(id+"F5.wireOp",EDGE,"E17.MirrorCS");var subQ1=sQuery(id+"F5.wireOp",EDGE,"E12.MirrorC");var subQ2=makeQuery(id+"F5.imprint","INTERSECT",VERTEX,{"disambiguationData":[OD(0.0)],"derivedFrom":[subQ1,subQ0]});Q14=makeQuery(id+"F5.imprint","IMPRINT",FACE,{"disambiguationData":[TD([[makeQuery(id+"F5.imprint","IMPRINT",EDGE,{"disambiguationData":[TD([[subQ2,1.0]])],"derivedFrom":subQ1}),-1.0]])]});}
            var Q15;
            Q15=sQuery(id+"F5.wireOp",EDGE,"E22.MirrorC");
            var Q16;
            Q16=sQuery(id+"F5.wireOp",EDGE,"E21.MirrorC");
            var Q17;
            Q17=sQuery(id+"F5.wireOp",EDGE,"E19.MirrorC");
            var Q18;
            Q18=sQuery(id+"F5.wireOp",EDGE,"E25.MirrorC");
            var Q19;
            Q19=sQuery(id+"F5.wireOp",EDGE,"E13.MirrorC");
            var Q20;
            Q20=sQuery(id+"F5.wireOp",EDGE,"E11.MirrorC");
            var Q21;
            Q21=sQuery(id+"F5.wireOp",EDGE,"E16.MirrorC");
            var Q22;
            Q22=sQuery(id+"F5.wireOp",EDGE,"E14.MirrorC");
            var Q23;
            Q23=sQuery(id+"F5.wireOp",EDGE,"E24.MirrorC");
            var Q24;
            Q24=sQuery(id+"F5.wireOp",EDGE,"E12.MirrorC");
            extrude(context, id + "F26", {"entities" : qUnion([Q0, Q1, Q2, Q3, Q4, Q5, Q6, Q7, Q8, Q9, Q10, Q11, Q12, Q13, Q14]), "operationType" : NewBodyOperationType.ADD, "surfaceEntities" : qUnion([Q15, Q16, Q17, Q18, Q19, Q20, Q21, Q22, Q23, Q24]), "depth" : .8 * mm, "offsetDistance" : 25 * mm});
        }
        {
            var Q0;
            {var subQ0=sQuery(id+"F5.wireOp",EDGE,"E9.left");var subQ1=sQuery(id+"F5.wireOp",EDGE,"E10");var subQ2=makeQuery(id+"F5.imprint","INTERSECT",VERTEX,{"disambiguationData":[OD(0.0)],"derivedFrom":[subQ1,subQ0]});Q0=makeQuery(id+"F5.imprint","IMPRINT",FACE,{"disambiguationData":[TD([[makeQuery(id+"F5.imprint","IMPRINT",EDGE,{"disambiguationData":[TD([[subQ2,-1.0]])],"derivedFrom":subQ1}),-1.0]])]});}
            var Q1;
            Q1=makeQuery(id+"F5.imprint","IMPRINT",FACE,{"disambiguationData":[TD([[makeQuery(id+"F5.imprint","IMPRINT",EDGE,{"derivedFrom":sQuery(id+"F5.wireOp",EDGE,"E23.MirrorC")}),-1.0]])]});
            var Q2;
            Q2=makeQuery(id+"F5.imprint","IMPRINT",FACE,{"disambiguationData":[TD([[makeQuery(id+"F5.imprint","IMPRINT",EDGE,{"derivedFrom":sQuery(id+"F5.wireOp",EDGE,"E15.MirrorC")}),-1.0]])]});
            var Q3;
            Q3=makeQuery(id+"F5.imprint","IMPRINT",FACE,{"disambiguationData":[TD([[makeQuery(id+"F5.imprint","IMPRINT",EDGE,{"derivedFrom":sQuery(id+"F5.wireOp",EDGE,"E18.MirrorC")}),-1.0]])]});
            extrude(context, id + "F27", {"entities" : qUnion([Q0, Q1, Q2, Q3]), "operationType" : NewBodyOperationType.ADD, "depth" : 1.6 * mm, "offsetDistance" : 25 * mm});
        }
        {
            var Q0;
            Q0=makeQuery(id+"F20.boolean.opBoolean","COPY",FACE,{"derivedFrom":makeQuery(id+"F20.opExtrude","SWEPT_FACE",FACE,{"disambiguationData":[OSD([sQuery(id+"F19.wireOp",EDGE,"E47")])]})});
            var sketch = newSketch(context, id + "F28", { "sketchPlane" : qUnion([Q0])});
            skCircle(sketch, "E53", {"center": v(12.99, -4.62) * mm, "radius": 0.8 * mm});
            skSolve(sketch);
        }
        {
            var Q0;
            {var subQ0=sQuery(id+"F28.wireOp",EDGE,"E53");var subQ1=makeQuery(id+"F20.boolean.opBoolean","COPY",EDGE,{"derivedFrom":makeQuery(id+"F20.opExtrude","SWEPT_EDGE",EDGE,{"disambiguationData":[OSD([sQuery(id+"F19.wireOp",EDGE,"E47"),sQuery(id+"F19.wireOp",EDGE,"E48")])]})});var subQ2=makeQuery(id+"F28.imprint","INTERSECT",VERTEX,{"disambiguationData":[OD(0.0)],"derivedFrom":[subQ1,subQ0]});Q0=makeQuery(id+"F28.imprint","IMPRINT",FACE,{"disambiguationData":[TD([[makeQuery(id+"F28.imprint","IMPRINT",EDGE,{"disambiguationData":[TD([[subQ2,-1.0]])],"derivedFrom":subQ0}),1.0]])]});}
            extrude(context, id + "F29", {"entities" : qUnion([Q0]), "depth" : .8 * mm, "offsetDistance" : 25 * mm});
        }
        {
            var Q0;
            Q0=makeQuery(id+"F29.opExtrude","CAP_EDGE",EDGE,{"disambiguationData":[OSD([sQuery(id+"F28.wireOp",EDGE,"E53")])],"isStart":false});
            fillet(context, id + "F30", {"entities" : qUnion([Q0]), "tangentPropagation" : true, "radius" : .5 * mm, "defaultsChanged" : false, "vertexSettings" : [], "allowEdgeOverflow" : false});
        }
        {
            var Q0;
            Q0=makeQuery(id+"F29.opExtrude","SWEPT_BODY",BODY,{"disambiguationData":[OSD([sQuery(id+"F19.wireOp",EDGE,"E47"),sQuery(id+"F19.wireOp",EDGE,"E48"),sQuery(id+"F28.wireOp",EDGE,"E53")])]});
            var Q1;
            {var subQ0=sQuery(id+"F0.wireOp",EDGE,"E0.bottom");var subQ2=sQuery(id+"F0.wireOp",EDGE,"E0.right");var subQ3=sQuery(id+"F11.wireOp",EDGE,"E39.left");Q1=makeQuery(id+"F20.boolean.opBoolean","SPLIT",EDGE,{"disambiguationData":[TD([makeQuery(id+"F12.opExtrude","SWEPT_FACE",FACE,{"disambiguationData":[OSD([subQ3])]})])],"derivedFrom":makeQuery(id+"F1.opRevolve","SWEPT_EDGE",EDGE,{"disambiguationData":[OSD([subQ0,subQ2])]})});}
            circularPattern(context, id + "F31", {"entities" : qUnion([Q0]), "axis" : qUnion([Q1]), "angle" : 55 * degree, "instanceCount" : 4, "equalSpace" : true, "computeTransformsWithoutBuiltin" : true});
        }
        {
            var Q0;
            Q0=makeQuery(id+"F26.opExtrude","CAP_EDGE",EDGE,{"disambiguationData":[OSD([sQuery(id+"F5.wireOp",EDGE,"E12.MirrorC")])],"isStart":false});
            var Q1;
            Q1=makeQuery(id+"F26.opExtrude","CAP_EDGE",EDGE,{"disambiguationData":[OSD([sQuery(id+"F5.wireOp",EDGE,"E24.MirrorC")])],"isStart":false});
            var Q2;
            Q2=makeQuery(id+"F26.opExtrude","CAP_EDGE",EDGE,{"disambiguationData":[OSD([sQuery(id+"F5.wireOp",EDGE,"E14.MirrorC")])],"isStart":false});
            var Q3;
            Q3=makeQuery(id+"F26.opExtrude","CAP_EDGE",EDGE,{"disambiguationData":[OSD([sQuery(id+"F5.wireOp",EDGE,"E16.MirrorC")])],"isStart":false});
            var Q4;
            Q4=makeQuery(id+"F26.opExtrude","CAP_EDGE",EDGE,{"disambiguationData":[OSD([sQuery(id+"F5.wireOp",EDGE,"E11.MirrorC")])],"isStart":false});
            var Q5;
            Q5=makeQuery(id+"F26.opExtrude","CAP_EDGE",EDGE,{"disambiguationData":[OSD([sQuery(id+"F5.wireOp",EDGE,"E13.MirrorC")])],"isStart":false});
            var Q6;
            Q6=makeQuery(id+"F26.opExtrude","CAP_EDGE",EDGE,{"disambiguationData":[OSD([sQuery(id+"F5.wireOp",EDGE,"E25.MirrorC")])],"isStart":false});
            var Q7;
            Q7=makeQuery(id+"F26.opExtrude","CAP_EDGE",EDGE,{"disambiguationData":[OSD([sQuery(id+"F5.wireOp",EDGE,"E19.MirrorC")])],"isStart":false});
            var Q8;
            Q8=makeQuery(id+"F26.opExtrude","CAP_EDGE",EDGE,{"disambiguationData":[OSD([sQuery(id+"F5.wireOp",EDGE,"E21.MirrorC")])],"isStart":false});
            var Q9;
            Q9=makeQuery(id+"F26.opExtrude","CAP_EDGE",EDGE,{"disambiguationData":[OSD([sQuery(id+"F5.wireOp",EDGE,"E22.MirrorC")])],"isStart":false});
            var Q10;
            Q10=makeQuery(id+"F27.opExtrude","CAP_EDGE",EDGE,{"disambiguationData":[OSD([sQuery(id+"F5.wireOp",EDGE,"E23.MirrorC")])],"isStart":false});
            var Q11;
            Q11=makeQuery(id+"F27.opExtrude","CAP_EDGE",EDGE,{"disambiguationData":[OSD([sQuery(id+"F5.wireOp",EDGE,"E18.MirrorC")])],"isStart":false});
            var Q12;
            Q12=makeQuery(id+"F27.opExtrude","CAP_EDGE",EDGE,{"disambiguationData":[OSD([sQuery(id+"F5.wireOp",EDGE,"E15.MirrorC")])],"isStart":false});
            var Q13;
            Q13=makeQuery(id+"F27.opExtrude","CAP_EDGE",EDGE,{"disambiguationData":[OSD([sQuery(id+"F5.wireOp",EDGE,"E10")])],"isStart":false});
            fillet(context, id + "F32", {"entities" : qUnion([Q0, Q1, Q2, Q3, Q4, Q5, Q6, Q7, Q8, Q9, Q10, Q11, Q12, Q13]), "tangentPropagation" : true, "radius" : .4 * mm, "defaultsChanged" : true, "vertexSettings" : [], "allowEdgeOverflow" : false});
        }
        {
            var Q0;
            Q0=makeQuery(id+"F1.opRevolve","SWEPT_BODY",BODY,{"disambiguationData":[OSD([sQuery(id+"F0.wireOp",EDGE,"E0.bottom"),sQuery(id+"F0.wireOp",EDGE,"E0.top"),sQuery(id+"F0.wireOp",EDGE,"E0.left"),sQuery(id+"F0.wireOp",EDGE,"E0.right"),sQuery(id+"F0.wireOp",EDGE,"E1.top"),sQuery(id+"F0.wireOp",EDGE,"E1.right"),sQuery(id+"F0.wireOp",EDGE,"E3"),sQuery(id+"F0.wireOp",EDGE,"E4"),sQuery(id+"F0.wireOp",EDGE,"E5.bottom"),sQuery(id+"F0.wireOp",EDGE,"E5.top"),sQuery(id+"F0.wireOp",EDGE,"E5.right")])]});
            var Q1;
            Q1=makeQuery(id+"F0.imprint","IMPRINT",FACE,{"disambiguationData":[TD([[makeQuery(id+"F0.imprint","IMPRINT",EDGE,{"derivedFrom":sQuery(id+"F0.wireOp",EDGE,"E5.bottom")}),1.0]])]});
            mirror(context, id + "F33", {"entities" : qUnion([Q0]), "mirrorPlane" : qUnion([Q1])});
        }
        {
            var Q0;
            Q0=makeQuery(id+"F1.opRevolve","SWEPT_BODY",BODY,{"disambiguationData":[OSD([sQuery(id+"F0.wireOp",EDGE,"E0.bottom"),sQuery(id+"F0.wireOp",EDGE,"E0.top"),sQuery(id+"F0.wireOp",EDGE,"E0.left"),sQuery(id+"F0.wireOp",EDGE,"E0.right"),sQuery(id+"F0.wireOp",EDGE,"E1.top"),sQuery(id+"F0.wireOp",EDGE,"E1.right"),sQuery(id+"F0.wireOp",EDGE,"E3"),sQuery(id+"F0.wireOp",EDGE,"E4"),sQuery(id+"F0.wireOp",EDGE,"E5.bottom"),sQuery(id+"F0.wireOp",EDGE,"E5.top"),sQuery(id+"F0.wireOp",EDGE,"E5.right")])]});
            var Q1;
            Q1=makeQuery(id+"F4.opExtrude","SWEPT_BODY",BODY,{"disambiguationData":[OSD([sQuery(id+"F3.wireOp",EDGE,"E6"),sQuery(id+"F3.wireOp",EDGE,"E7"),sQuery(id+"F3.wireOp",EDGE,"E8")])]});
            var Q2;
            Q2=makeQuery(id+"F1Xjq86WKhaPot2_3.opPattern","COPY",BODY,{"derivedFrom":makeQuery(id+"FC4CTspH2qNEnUw_2.opExtrude","SWEPT_BODY",BODY,{"disambiguationData":[OSD([sQuery(id+"F1NFxzLEQe7orcR_2.wireOp",EDGE,"FOGVbPp3-W0lZ-WL5a-hbK7-i5BhFczB104l")])]}),"instanceName":"1"});
            var Q3;
            Q3=makeQuery(id+"FE02PZ1V3YkT8Zu_3.opExtrude","SWEPT_BODY",BODY,{"disambiguationData":[OSD([sQuery(id+"F021Rv2FwfjDZFp_3.wireOp",EDGE,"ssReJOMJ-1Qrg-lFMj-15ix-001Sl4pRNQd3"),sQuery(id+"F021Rv2FwfjDZFp_3.wireOp",EDGE,"z5rMjA4P-JcQ4-gkdB-odXw-3UHxNwSVD4uy"),sQuery(id+"F021Rv2FwfjDZFp_3.wireOp",EDGE,"Wds6SQ0y-bdoS-YevH-0Kbp-UmnE9QZR5nlf"),sQuery(id+"F021Rv2FwfjDZFp_3.wireOp",EDGE,"Co5j3mE5-LpF4-ztqA-Cjt6-Q5TmkK1vIlKz"),sQuery(id+"F021Rv2FwfjDZFp_3.wireOp",EDGE,"3SdRo5C6-dzbK-MITp-01Az-ImDg15YoQx3z")])]});
            var Q4;
            Q4=makeQuery(id+"F1Xjq86WKhaPot2_3.opPattern","COPY",BODY,{"derivedFrom":makeQuery(id+"FC4CTspH2qNEnUw_2.opExtrude","SWEPT_BODY",BODY,{"disambiguationData":[OSD([sQuery(id+"F1NFxzLEQe7orcR_2.wireOp",EDGE,"FOGVbPp3-W0lZ-WL5a-hbK7-i5BhFczB104l")])]}),"instanceName":"2"});
            var Q5;
            Q5=makeQuery(id+"F33.opPattern","COPY",BODY,{"derivedFrom":makeQuery(id+"F1.opRevolve","SWEPT_BODY",BODY,{"disambiguationData":[OSD([sQuery(id+"F0.wireOp",EDGE,"E0.bottom"),sQuery(id+"F0.wireOp",EDGE,"E0.top"),sQuery(id+"F0.wireOp",EDGE,"E0.left"),sQuery(id+"F0.wireOp",EDGE,"E0.right"),sQuery(id+"F0.wireOp",EDGE,"E1.top"),sQuery(id+"F0.wireOp",EDGE,"E1.right"),sQuery(id+"F0.wireOp",EDGE,"E3"),sQuery(id+"F0.wireOp",EDGE,"E4"),sQuery(id+"F0.wireOp",EDGE,"E5.bottom"),sQuery(id+"F0.wireOp",EDGE,"E5.top"),sQuery(id+"F0.wireOp",EDGE,"E5.right")])]}),"instanceName":"1"});
            var Q6;
            Q6=makeQuery(id+"F1Xjq86WKhaPot2_3.opPattern","COPY",BODY,{"derivedFrom":makeQuery(id+"FC4CTspH2qNEnUw_2.opExtrude","SWEPT_BODY",BODY,{"disambiguationData":[OSD([sQuery(id+"F1NFxzLEQe7orcR_2.wireOp",EDGE,"FOGVbPp3-W0lZ-WL5a-hbK7-i5BhFczB104l")])]}),"instanceName":"3"});
            var Q7;
            Q7=makeQuery(id+"F1Xjq86WKhaPot2_3.opPattern","COPY",BODY,{"derivedFrom":makeQuery(id+"FC4CTspH2qNEnUw_2.opExtrude","SWEPT_BODY",BODY,{"disambiguationData":[OSD([sQuery(id+"F1NFxzLEQe7orcR_2.wireOp",EDGE,"FOGVbPp3-W0lZ-WL5a-hbK7-i5BhFczB104l")])]}),"instanceName":"4"});
            var Q8;
            Q8=makeQuery(id+"F33.opPattern","COPY",BODY,{"derivedFrom":makeQuery(id+"F4.opExtrude","SWEPT_BODY",BODY,{"disambiguationData":[OSD([sQuery(id+"F3.wireOp",EDGE,"E6"),sQuery(id+"F3.wireOp",EDGE,"E7"),sQuery(id+"F3.wireOp",EDGE,"E8")])]}),"instanceName":"1"});
            var Q9;
            Q9=makeQuery(id+"F33.opPattern","COPY",BODY,{"derivedFrom":makeQuery(id+"FE02PZ1V3YkT8Zu_3.opExtrude","SWEPT_BODY",BODY,{"disambiguationData":[OSD([sQuery(id+"F021Rv2FwfjDZFp_3.wireOp",EDGE,"ssReJOMJ-1Qrg-lFMj-15ix-001Sl4pRNQd3"),sQuery(id+"F021Rv2FwfjDZFp_3.wireOp",EDGE,"z5rMjA4P-JcQ4-gkdB-odXw-3UHxNwSVD4uy"),sQuery(id+"F021Rv2FwfjDZFp_3.wireOp",EDGE,"Wds6SQ0y-bdoS-YevH-0Kbp-UmnE9QZR5nlf"),sQuery(id+"F021Rv2FwfjDZFp_3.wireOp",EDGE,"Co5j3mE5-LpF4-ztqA-Cjt6-Q5TmkK1vIlKz"),sQuery(id+"F021Rv2FwfjDZFp_3.wireOp",EDGE,"3SdRo5C6-dzbK-MITp-01Az-ImDg15YoQx3z")])]}),"instanceName":"1"});
            var Q10;
            Q10=makeQuery(id+"FC4CTspH2qNEnUw_2.opExtrude","SWEPT_BODY",BODY,{"disambiguationData":[OSD([sQuery(id+"F1NFxzLEQe7orcR_2.wireOp",EDGE,"FOGVbPp3-W0lZ-WL5a-hbK7-i5BhFczB104l")])]});
            var Q11;
            Q11=makeQuery(id+"F33.opPattern","COPY",BODY,{"derivedFrom":makeQuery(id+"FC4CTspH2qNEnUw_2.opExtrude","SWEPT_BODY",BODY,{"disambiguationData":[OSD([sQuery(id+"F1NFxzLEQe7orcR_2.wireOp",EDGE,"FOGVbPp3-W0lZ-WL5a-hbK7-i5BhFczB104l")])]}),"instanceName":"1"});
            var Q12;
            Q12=makeQuery(id+"F33.opPattern","COPY",BODY,{"derivedFrom":makeQuery(id+"F1Xjq86WKhaPot2_3.opPattern","COPY",BODY,{"derivedFrom":makeQuery(id+"FC4CTspH2qNEnUw_2.opExtrude","SWEPT_BODY",BODY,{"disambiguationData":[OSD([sQuery(id+"F1NFxzLEQe7orcR_2.wireOp",EDGE,"FOGVbPp3-W0lZ-WL5a-hbK7-i5BhFczB104l")])]}),"instanceName":"1"}),"instanceName":"1"});
            var Q13;
            Q13=makeQuery(id+"F33.opPattern","COPY",BODY,{"derivedFrom":makeQuery(id+"F1Xjq86WKhaPot2_3.opPattern","COPY",BODY,{"derivedFrom":makeQuery(id+"FC4CTspH2qNEnUw_2.opExtrude","SWEPT_BODY",BODY,{"disambiguationData":[OSD([sQuery(id+"F1NFxzLEQe7orcR_2.wireOp",EDGE,"FOGVbPp3-W0lZ-WL5a-hbK7-i5BhFczB104l")])]}),"instanceName":"2"}),"instanceName":"1"});
            var Q14;
            Q14=makeQuery(id+"F33.opPattern","COPY",BODY,{"derivedFrom":makeQuery(id+"F1Xjq86WKhaPot2_3.opPattern","COPY",BODY,{"derivedFrom":makeQuery(id+"FC4CTspH2qNEnUw_2.opExtrude","SWEPT_BODY",BODY,{"disambiguationData":[OSD([sQuery(id+"F1NFxzLEQe7orcR_2.wireOp",EDGE,"FOGVbPp3-W0lZ-WL5a-hbK7-i5BhFczB104l")])]}),"instanceName":"3"}),"instanceName":"1"});
            var Q15;
            Q15=makeQuery(id+"F33.opPattern","COPY",BODY,{"derivedFrom":makeQuery(id+"F1Xjq86WKhaPot2_3.opPattern","COPY",BODY,{"derivedFrom":makeQuery(id+"FC4CTspH2qNEnUw_2.opExtrude","SWEPT_BODY",BODY,{"disambiguationData":[OSD([sQuery(id+"F1NFxzLEQe7orcR_2.wireOp",EDGE,"FOGVbPp3-W0lZ-WL5a-hbK7-i5BhFczB104l")])]}),"instanceName":"4"}),"instanceName":"1"});
            var Q16;
            {var subQ0=sQuery(id+"F0.wireOp",EDGE,"E0.top");Q16=makeQuery(id+"F33.opPattern","COPY",FACE,{"derivedFrom":makeQuery(id+"F2.boolean.opBoolean","MERGE",FACE,{"derivedFrom":[makeQuery(id+"F1.opRevolve","SWEPT_FACE",FACE,{"disambiguationData":[OSD([subQ0])]}),makeQuery(id+"F2.opExtrude","SWEPT_FACE",FACE,{"disambiguationData":[OSD([subQ0])]})]}),"instanceName":"1"});}
            mirror(context, id + "F34", {"entities" : qUnion([Q0, Q1, Q2, Q3, Q4, Q5, Q6, Q7, Q8, Q9, Q10, Q11, Q12, Q13, Q14, Q15]), "mirrorPlane" : qUnion([Q16])});
        }
    });
